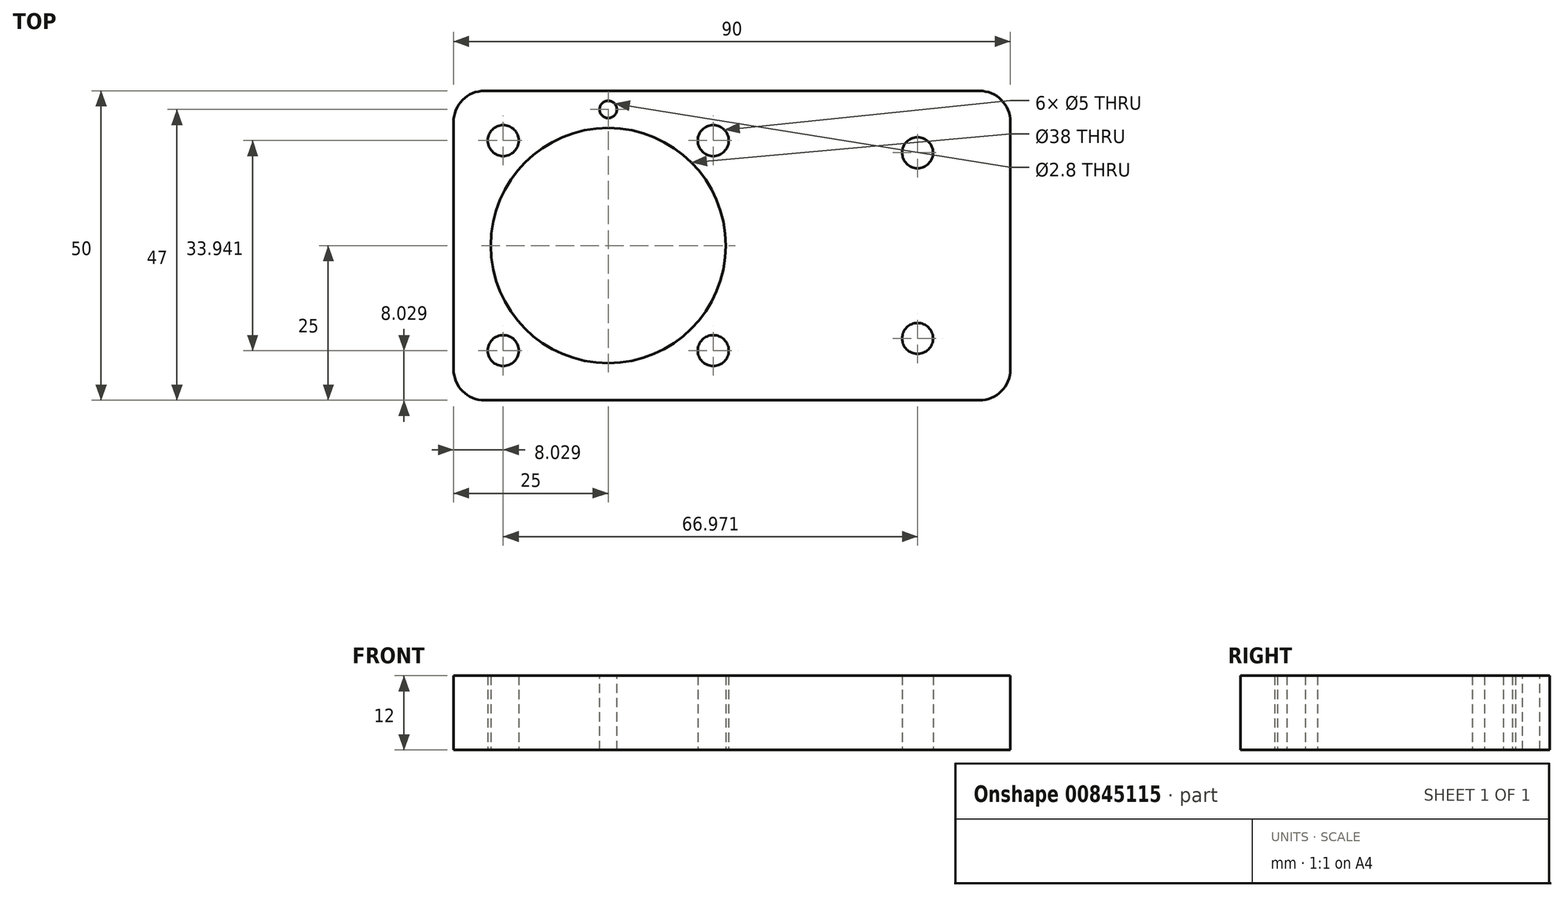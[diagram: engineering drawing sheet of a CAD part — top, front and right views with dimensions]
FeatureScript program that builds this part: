
annotation { "Feature Type Name" : "Feature", "Feature Type Description" : "" }
export const myFeature = defineFeature(function(context is Context, id is Id, definition is map)
    precondition{}
    {
        {
            var Q0;
            Q0=qCreatedBy(makeId("Top.planeOp"),FACE);
            var sketch = newSketch(context, id + "F0", { "sketchPlane" : qUnion([Q0])});
            skLineSegment(sketch, "E0.bottom", {"start": v(25, 25) * mm, "end": v(-25, 25) * mm});
            skLineSegment(sketch, "E0.top", {"start": v(25, -25) * mm, "end": v(-25, -25) * mm});
            skLineSegment(sketch, "E0.left", {"start": v(25, 25) * mm, "end": v(25, -25) * mm});
            skLineSegment(sketch, "E0.right", {"start": v(-25, 25) * mm, "end": v(-25, -25) * mm});
            skPoint(sketch, "E0.middle", {"position": v(0, 0) * mm});
            skCircle(sketch, "E1", {"center": v(0, 0) * mm, "radius": 24 * mm, "construction": true});
            skLineSegment(sketch, "E2.bottom", {"start": v(21, -21) * mm, "end": v(-21, -21) * mm, "construction": true});
            skLineSegment(sketch, "E2.top", {"start": v(21, 21) * mm, "end": v(-21, 21) * mm, "construction": true});
            skLineSegment(sketch, "E2.left", {"start": v(21, -21) * mm, "end": v(21, 21) * mm, "construction": true});
            skLineSegment(sketch, "E2.right", {"start": v(-21, -21) * mm, "end": v(-21, 21) * mm, "construction": true});
            skLineSegment(sketch, "E3", {"start": v(-21, 21) * mm, "end": v(25, -25) * mm, "construction": true});
            skLineSegment(sketch, "E4", {"start": v(21, 21) * mm, "end": v(-25, -25) * mm, "construction": true});
            skCircle(sketch, "E5", {"center": v(-16.97, 16.97) * mm, "radius": 2.5 * mm});
            skCircle(sketch, "E6", {"center": v(16.97, 16.97) * mm, "radius": 2.5 * mm});
            skCircle(sketch, "E7", {"center": v(16.97, -16.97) * mm, "radius": 2.5 * mm});
            skCircle(sketch, "E8", {"center": v(-16.97, -16.97) * mm, "radius": 2.5 * mm});
            skCircle(sketch, "E9", {"center": v(0, 0) * mm, "radius": 19 * mm});
            skCircle(sketch, "E10", {"center": v(0, 0) * mm, "radius": 15 * mm, "construction": true});
            skLineSegment(sketch, "E11.bottom", {"start": v(25, -25) * mm, "end": v(65, -25) * mm});
            skLineSegment(sketch, "E11.top", {"start": v(25, 25) * mm, "end": v(65, 25) * mm});
            skLineSegment(sketch, "E11.left", {"start": v(25, -25) * mm, "end": v(25, 25) * mm});
            skLineSegment(sketch, "E11.right", {"start": v(65, -25) * mm, "end": v(65, 25) * mm});
            skLineSegment(sketch, "E12", {"start": v(50, 25) * mm, "end": v(50, -25) * mm, "construction": true});
            skLineSegment(sketch, "E13", {"start": v(25, -15) * mm, "end": v(65, -15) * mm, "construction": true});
            skLineSegment(sketch, "E14", {"start": v(25, 15) * mm, "end": v(65, 15) * mm, "construction": true});
            skCircle(sketch, "E15", {"center": v(50, 15) * mm, "radius": 2.5 * mm});
            skCircle(sketch, "E16", {"center": v(50, -15) * mm, "radius": 2.5 * mm});
            skSolve(sketch);
        }
        {
            var Q0;
            Q0 = qSketchRegion(id + "F0", true);
            extrude(context, id + "F1", {"entities" : qUnion([Q0]), "depth" : 12 * mm, "offsetDistance" : 25 * mm});
        }
        {
            var Q0;
            Q0=makeQuery(id+"F1.opExtrude","CAP_FACE",FACE,{"disambiguationData":[OSD([sQuery(id+"F0.wireOp",EDGE,"E0.bottom"),sQuery(id+"F0.wireOp",EDGE,"E0.top"),sQuery(id+"F0.wireOp",EDGE,"E0.right"),sQuery(id+"F0.wireOp",EDGE,"E5"),sQuery(id+"F0.wireOp",EDGE,"E6"),sQuery(id+"F0.wireOp",EDGE,"E7"),sQuery(id+"F0.wireOp",EDGE,"E8"),sQuery(id+"F0.wireOp",EDGE,"E9"),sQuery(id+"F0.wireOp",EDGE,"E11.bottom"),sQuery(id+"F0.wireOp",EDGE,"E11.top"),sQuery(id+"F0.wireOp",EDGE,"E11.right"),sQuery(id+"F0.wireOp",EDGE,"naur5PNt-FYEl-odex-y8Rd-N0yxZ2Jzk4IH"),sQuery(id+"F0.wireOp",EDGE,"DLWSIOgS-RGDa-Mndz-yOIL-QEmDsBVwLk5P")])],"isStart":false});
            var sketch = newSketch(context, id + "F2", { "sketchPlane" : qUnion([Q0])});
            skCircle(sketch, "E17", {"center": v(0, 22) * mm, "radius": 1.4 * mm});
            skSolve(sketch);
        }
        {
            var Q0;
            Q0 = qSketchRegion(id + "F2", true);
            extrude(context, id + "F3", {"entities" : qUnion([Q0]), "operationType" : NewBodyOperationType.REMOVE, "endBound" : BoundingType.THROUGH_ALL, "oppositeDirection" : true, "depth" : 25 * mm, "offsetDistance" : 25 * mm});
        }
        {
            var Q0;
            Q0=makeQuery(id+"F1.opExtrude","SWEPT_EDGE",EDGE,{"disambiguationData":[OSD([sQuery(id+"F0.wireOp",EDGE,"E11.bottom"),sQuery(id+"F0.wireOp",EDGE,"E11.right")])]});
            var Q1;
            Q1=makeQuery(id+"F1.opExtrude","SWEPT_EDGE",EDGE,{"disambiguationData":[OSD([sQuery(id+"F0.wireOp",EDGE,"E0.top"),sQuery(id+"F0.wireOp",EDGE,"E0.right")])]});
            var Q2;
            Q2=makeQuery(id+"F1.opExtrude","SWEPT_EDGE",EDGE,{"disambiguationData":[OSD([sQuery(id+"F0.wireOp",EDGE,"E0.bottom"),sQuery(id+"F0.wireOp",EDGE,"E0.right")])]});
            var Q3;
            Q3=makeQuery(id+"F1.opExtrude","SWEPT_EDGE",EDGE,{"disambiguationData":[OSD([sQuery(id+"F0.wireOp",EDGE,"E11.top"),sQuery(id+"F0.wireOp",EDGE,"E11.right")])]});
            fillet(context, id + "F4", {"entities" : qUnion([Q0, Q1, Q2, Q3]), "radius" : 5 * mm, "tangentPropagation" : true, "allowEdgeOverflow" : false});
        }
    });
